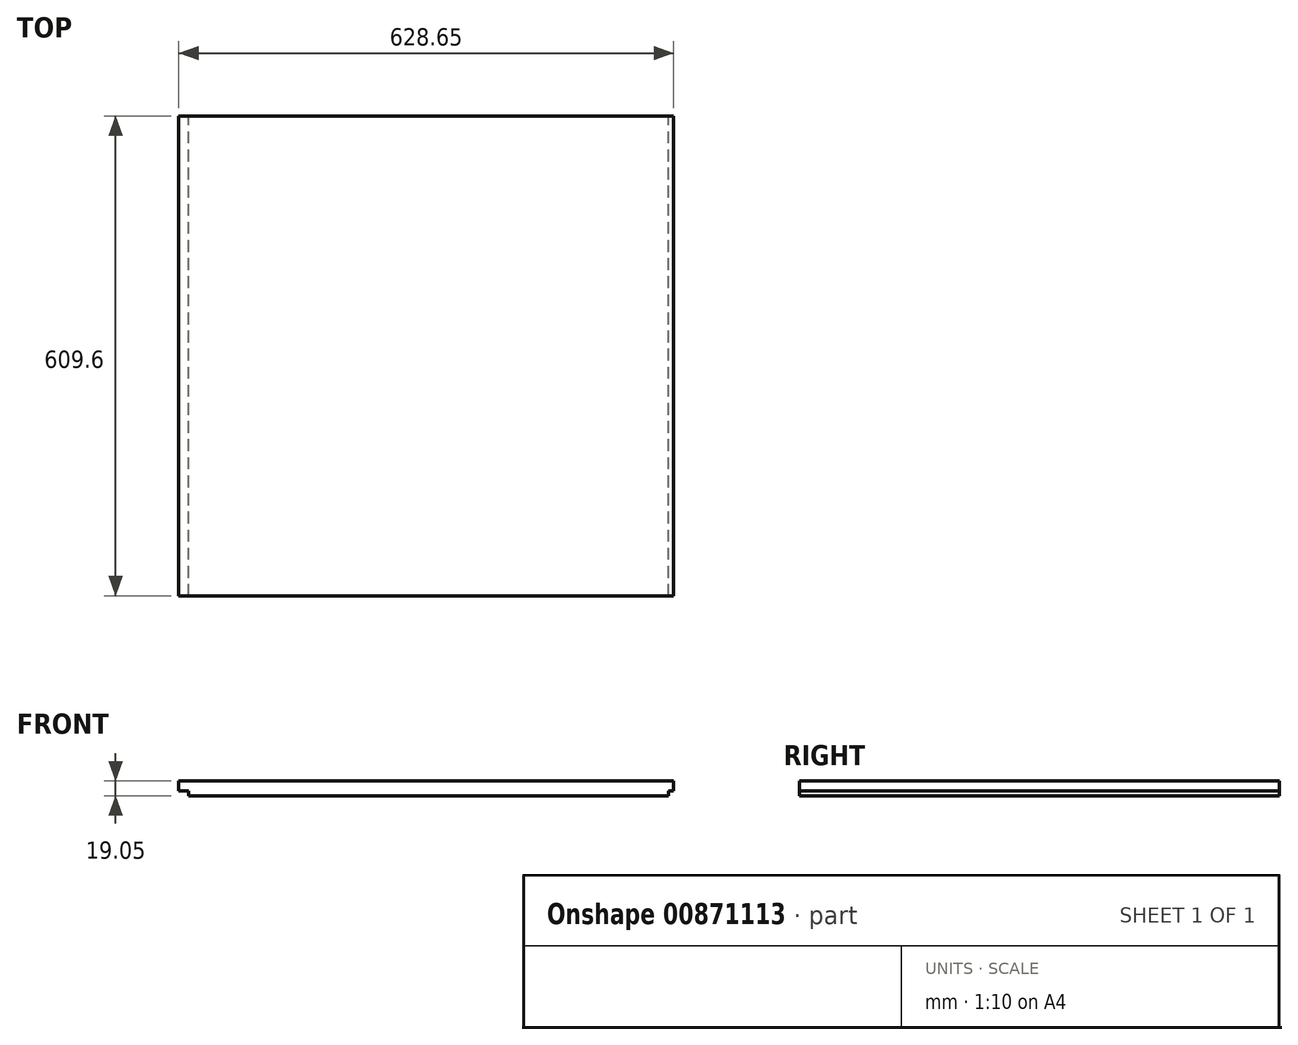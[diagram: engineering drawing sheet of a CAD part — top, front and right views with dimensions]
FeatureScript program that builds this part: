
annotation { "Feature Type Name" : "Feature", "Feature Type Description" : "" }
export const myFeature = defineFeature(function(context is Context, id is Id, definition is map)
    precondition{}
    {
        {
            var Q0;
            Q0=qCreatedBy(makeId("Front.planeOp"),FACE);
            var sketch = newSketch(context, id + "F0", { "sketchPlane" : qUnion([Q0])});
            skLineSegment(sketch, "E0.bottom", {"start": v(12.7, 0) * mm, "end": v(622.3, 0) * mm});
            skLineSegment(sketch, "E0.top", {"start": v(0, 19.05) * mm, "end": v(628.65, 19.05) * mm});
            skLineSegment(sketch, "E0.left", {"start": v(0, 6.35) * mm, "end": v(0, 19.05) * mm});
            skLineSegment(sketch, "E1.top", {"start": v(0, 6.35) * mm, "end": v(12.7, 6.35) * mm});
            skLineSegment(sketch, "E1.right", {"start": v(12.7, 0) * mm, "end": v(12.7, 6.35) * mm});
            skLineSegment(sketch, "E2.top", {"start": v(622.3, 6.35) * mm, "end": v(628.65, 6.35) * mm});
            skLineSegment(sketch, "E2.left", {"start": v(622.3, 0) * mm, "end": v(622.3, 6.35) * mm});
            skLineSegment(sketch, "E3", {"start": v(628.65, 6.35) * mm, "end": v(628.65, 19.05) * mm});
            skSolve(sketch);
        }
        {
            var Q0;
            Q0=qSketchRegion(id+"F0",true);
            extrude(context, id + "F1", {"entities" : qUnion([Q0]), "depth" : 609.6 * mm, "offsetDistance" : 25.4 * mm});
        }
    });
